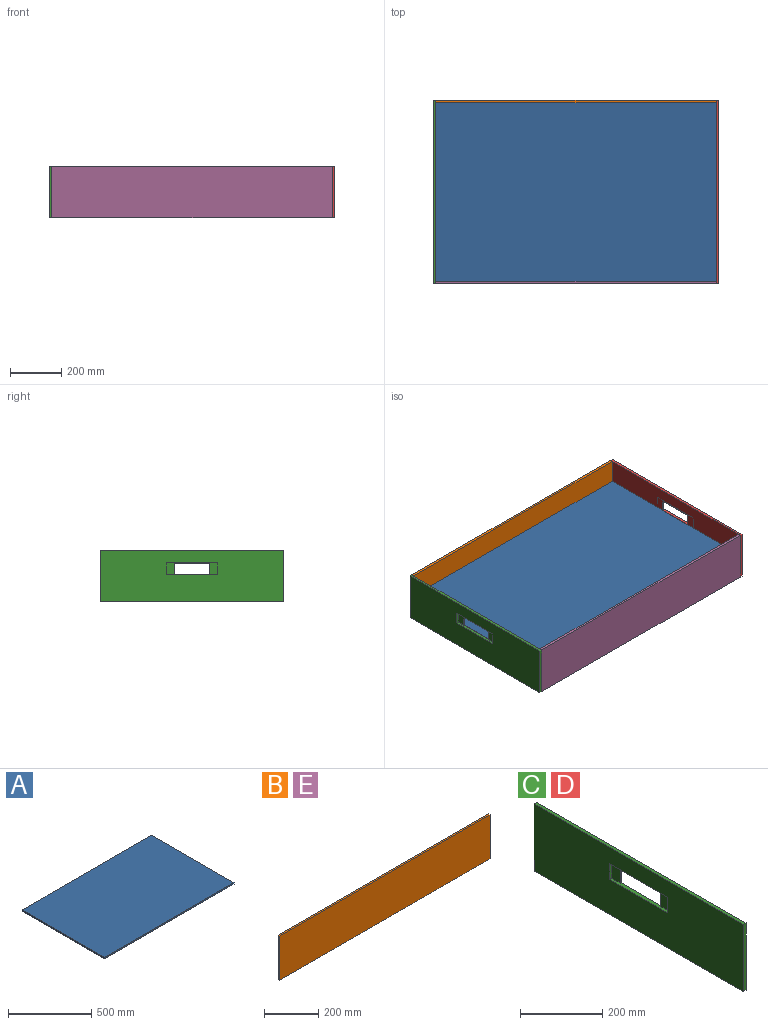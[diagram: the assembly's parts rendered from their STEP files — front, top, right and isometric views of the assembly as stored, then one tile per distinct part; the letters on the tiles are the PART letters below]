
ASSEMBLY  parts=5 mates=4
PART A: 6 faces, bbox 1100x700x10 mm
  f0: plane 1100x10mm, normal (0,1,0), area 11000mm2, adj f1,f3,f4,f5
  f1: plane 700x10mm, normal (-1,0,0), area 7000mm2, adj f0,f2,f4,f5
  f2: plane 1100x10mm, normal (0,-1,0), area 11000mm2, adj f1,f3,f4,f5
  f3: plane 700x10mm, normal (1,0,0), area 7000mm2, adj f0,f2,f4,f5
  f4: plane 1100x700mm, normal (0,0,1), area 770000mm2, adj f0,f1,f2,f3
  f5: plane 1100x700mm, normal (0,0,-1), area 770000mm2, adj f0,f1,f2,f3
PART B: 6 faces, bbox 1100x10x200 mm
  f0: plane 1100x10mm, normal (0,0,1), area 11000mm2, adj f1,f3,f4,f5
  f1: plane 200x10mm, normal (-1,0,0), area 2000mm2, adj f0,f2,f4,f5
  f2: plane 1100x10mm, normal (0,0,-1), area 11000mm2, adj f1,f3,f4,f5
  f3: plane 200x10mm, normal (1,0,0), area 2000mm2, adj f0,f2,f4,f5
  f4: plane 1100x200mm, normal (0,-1,0), area 220000mm2, adj f0,f1,f2,f3
  f5: plane 1100x200mm, normal (0,1,0), area 220000mm2, adj f0,f1,f2,f3
PART C: 14 faces, bbox 10x720x200 mm
  f0: plane 720x200mm, normal (-1,0,0), area 134600mm2, adj f5,f6,f7,f8,f9,f10,f11,f12
  f1: plane 45x3mm, normal (0,-1,0), area 135mm2, adj f2,f4,f9,f13
  f2: plane 140x3mm, normal (0,0,-1), area 420mm2, adj f1,f3,f4,f13
  f3: plane 45x3mm, normal (0,1,0), area 135mm2, adj f2,f4,f9,f13
  f4: plane 720x200mm, normal (1,0,0), area 137700mm2, adj f1,f2,f3,f5,f6,f7,f8,f9
  f5: plane 720x10mm, normal (0,0,1), area 7200mm2, adj f0,f4,f6,f8
  f6: plane 200x10mm, normal (0,-1,0), area 2000mm2, adj f0,f4,f5,f7
  f7: plane 720x10mm, normal (0,0,-1), area 7200mm2, adj f0,f4,f6,f8
  f8: plane 200x10mm, normal (0,1,0), area 2000mm2, adj f0,f4,f5,f7
  f9: plane 200x10mm, normal (0,0,1), area 1820mm2, adj f0,f1,f3,f4,f10,f11,f13
  f10: plane 47x7mm, normal (0,-1,0), area 329mm2, adj f0,f9,f12,f13
  f11: plane 47x7mm, normal (0,1,0), area 329mm2, adj f0,f9,f12,f13
  f12: plane 200x7mm, normal (0,0,-1), area 1400mm2, adj f0,f10,f11,f13
  f13: plane 200x47mm, normal (-1,0,0), area 3100mm2, adj f1,f2,f3,f9,f10,f11,f12
PART D: same geometry as C
PART E: same geometry as B
PLACE A at identity
PLACE B t=(0,360,5)mm
PLACE C t=(-560,0,5)mm
PLACE D rot(axis=(0,0,1),180deg) t=(560,0,5)mm
PLACE E t=(0,-350,5)mm
MATE fastened D.f4 <-> A.f3  axis (-1,0,0) through (550,0,10)mm
MATE fastened B.f4 <-> A.f0  axis (0,-1,0) through (0,350,5)mm
MATE fastened C.f4 <-> A.f1  axis (1,0,0) through (-550,0,10)mm
MATE fastened E.f5 <-> A.f2  axis (0,1,0) through (0,-350,5)mm
